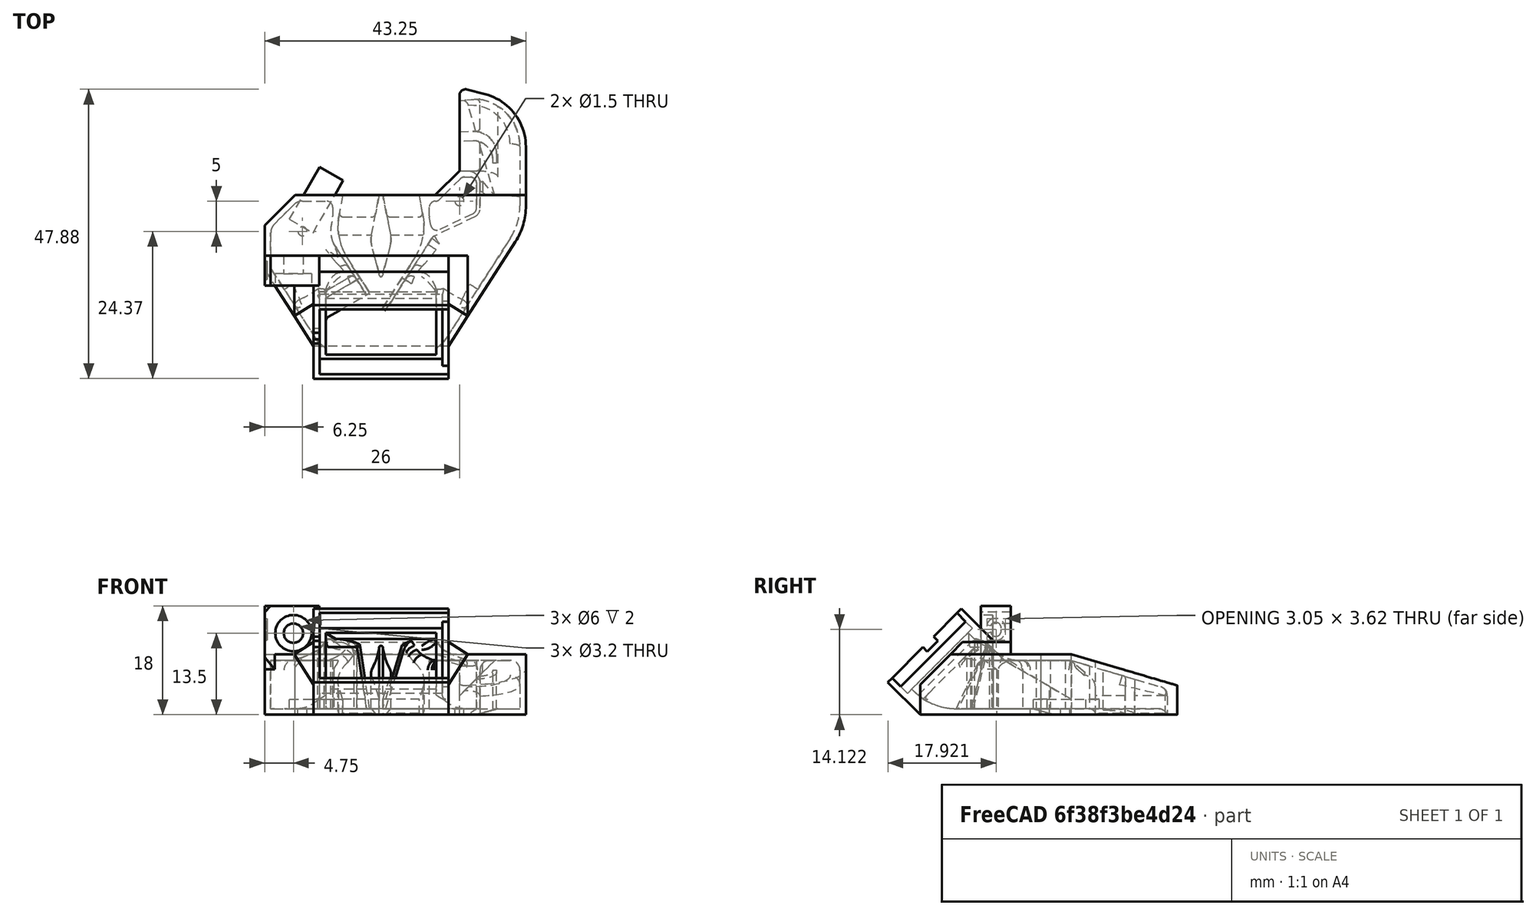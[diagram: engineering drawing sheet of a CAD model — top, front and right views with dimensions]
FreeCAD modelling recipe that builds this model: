
FCSTD DOCUMENT  (FreeCAD 0.18R16146 (Git))
Label: duct-lite
License: All rights reserved
LicenseURL: http://en.wikipedia.org/wiki/All_rights_reserved
objects: Part::Box×13, Part::Chamfer×8, Part::MultiFuse×8, Part::Cut×6, Part::Feature×5, Part::Cylinder×2, Part::Fillet×2
note: 44 computed .brp shape members not serialized (recipe doc carries the construction recipe); baked Part::Feature solids carry a one-line shape summary decoded from their .brp

FEATURE [Part::Feature] Part__Feature  label="RHD_nozzle_C_Final"
  Placement = pos=(0,0,0) rot=(1,0,0;1.5708rad)
  shape: bbox 48.02 x 47.91 x 18.02 mm, 273 faces (baked)
FEATURE [Part::Box] Box  label="Cube"
  AttacherType = Attacher::AttachEngine3D
  Height = 12
  Length = 23
  Placement = pos=(-29,4,0) rot=(0,0,1;0rad)
  Width = 21
FEATURE [Part::Box] Box001  label="Cube001"
  AttacherType = Attacher::AttachEngine3D
  Height = 19
  Length = 10
  Placement = pos=(-29.25,-13,0) rot=(0,0,1;0rad)
  Width = 23
FEATURE [Part::Box] Box002  label="Cube002"
  AttacherType = Attacher::AttachEngine3D
  Height = 12
  Length = 23
  Placement = pos=(-29,4,0) rot=(0,0,1;0rad)
  Width = 21
FEATURE [Part::Box] Box003  label="Cube003"
  AttacherType = Attacher::AttachEngine3D
  Height = 19
  Length = 10
  Placement = pos=(-29.25,-13,0) rot=(0,0,1;0rad)
  Width = 23
FEATURE [Part::Cut] Cut
  Base = -> Part__Feature
  Tool = -> Box002
FEATURE [Part::Cut] Cut001
  Base = -> Cut
  Tool = -> Box003
FEATURE [Part::Box] Box004  label="Cube004"
  AttacherType = Attacher::AttachEngine3D
  Height = 16
  Length = 10
  Placement = pos=(-24.25,-1,0) rot=(0,0,1;0rad)
  Width = 10
FEATURE [Part::Chamfer] Chamfer
  Base = -> Box004
  Edges = 1 edges r=5: [Edge5]
FEATURE [Part::Feature] Chamfer001
  shape: bbox 10 x 10 x 16 mm, 7 faces (baked)
FEATURE [Part::Cut] Cut002
  Base = -> Cut001
  Tool = -> Chamfer
FEATURE [Part::Box] Box005  label="Cube005"
  AttacherType = Attacher::AttachEngine3D
  Height = 10
  Length = 1
  Placement = pos=(-19.25,-7,0) rot=(0,0,1;0rad)
  Width = 6
FEATURE [Part::Box] Box006  label="Cube006"
  AttacherType = Attacher::AttachEngine3D
  Height = 10
  Length = 8
  Placement = pos=(-15,3,0) rot=(0,0,1;0rad)
  Width = 1
FEATURE [Part::Box] Box007  label="Cube007"
  AttacherType = Attacher::AttachEngine3D
  Height = 10
  Length = 8
  Placement = pos=(-19.3699,-2.52958,0) rot=(0,0,1;0.785398rad)
  Width = 1
FEATURE [Part::MultiFuse] Fusion001
  Shapes = -> [Chamfer001,Box,Box001]
FEATURE [Part::Cylinder] Cylinder
  Angle = 360
  AttacherType = Attacher::AttachEngine3D
  Height = 3
  Placement = pos=(-13,-2,0) rot=(0,0,1;0rad)
  Radius = 0.75
FEATURE [Part::Box] Box008  label="Cube008"
  AttacherType = Attacher::AttachEngine3D
  Height = 1.57
  Length = 4.5
  Placement = pos=(-15.1532,-0.0125771,1) rot=(0,0,-1;0.523599rad)
  Width = 10
FEATURE [Part::MultiFuse] Fusion
  Shapes = -> [Box005,Box007,Box006]
FEATURE [Part::Cut] Cut003
  Base = -> Fusion
  Tool = -> Fusion001
FEATURE [Part::Fillet] Fillet
  Base = -> Cut003
  Edges = 2 edges r=2: [Edge17,Edge31]
FEATURE [Part::Feature] Body001
  Placement = pos=(0,0,1) rot=(0,0,1;0rad)
  shape: bbox 12.23 x 12.68 x 8 mm, 3 faces (baked)
FEATURE [Part::Cut] Cut004
  Base = -> Cut002
  Tool = -> Body001
FEATURE [Part::Box] Box009  label="Cube009"
  AttacherType = Attacher::AttachEngine3D
  Height = 10
  Length = 1
  Placement = pos=(-19.25,-9,0) rot=(0,0,1;0rad)
  Width = 3
FEATURE [Part::Chamfer] Chamfer002
  Base = -> Box009
  Edges = 1 edges r=0.7: [Edge1]
FEATURE [Part::MultiFuse] Fusion002
  Shapes = -> [Fillet,Chamfer002]
FEATURE [Part::MultiFuse] Fusion003  label="stage-1"
  Shapes = -> [Cut004,Fusion002]
FEATURE [Part::Feature] Fusion003001  label="stage-1-rf"
  shape: bbox 43.62 x 47.91 x 18.02 mm, 215 faces (baked)
FEATURE [Part::Box] Box010  label="Cube010"
  AttacherType = Attacher::AttachEngine3D
  Height = 14
  Length = 7.5
  Placement = pos=(-10,-13.5,0) rot=(0,0,1;0.523599rad)
  Width = 1
FEATURE [Part::Box] Box011  label="Cube011"
  AttacherType = Attacher::AttachEngine3D
  Height = 12
  Length = 1
  Placement = pos=(-10.15,-22,0) rot=(0,0,1;0rad)
  Width = 10
FEATURE [Part::Chamfer] Chamfer003
  Base = -> Box011
  Edges = 1 edges r=1: [Edge9]
FEATURE [Part::Chamfer] Chamfer004
  Base = -> Chamfer003
  Edges = 1 edges r=8: [Edge8]
FEATURE [Part::Chamfer] Chamfer005
  Base = -> Box010
  Edges = 1 edges: [Edge2 r1=1.5 r2=1.8]
FEATURE [Part::Chamfer] Chamfer006
  Base = -> Chamfer005
  Edges = 1 edges: [Edge15 r1=4 r2=2]
FEATURE [Part::Box] Box012  label="Cube012"
  AttacherType = Attacher::AttachEngine3D
  Height = 1
  Length = 16
  Placement = pos=(-10,-19,0) rot=(0,0,1;0rad)
  Width = 10
FEATURE [Part::MultiFuse] Fusion003002
  Shapes = -> [Chamfer006,Box012]
FEATURE [Part::Chamfer] Chamfer007
  Base = -> Fusion003002
  Edges = 1 edges: [Edge5 r1=2.94 r2=10.2]
FEATURE [Part::MultiFuse] Fusion003003
  Shapes = -> [Chamfer004,Chamfer007]
FEATURE [Part::Fillet] Fillet001
  Base = -> Fusion003003
  Edges = 1 edges r=1: [Edge26]
FEATURE [Part::MultiFuse] Fusion003004  label="stage-2"
  Shapes = -> [Fusion003001,Fillet001]
FEATURE [Part::Feature] Fusion003004001  label="stage-2-rf"
  shape: bbox 43.62 x 47.91 x 18.02 mm, 240 faces (baked)
FEATURE [Part::Cylinder] Cylinder001
  Angle = 360
  AttacherType = Attacher::AttachEngine3D
  Height = 3
  Placement = pos=(13,3,0) rot=(0,0,1;0rad)
  Radius = 0.75
FEATURE [Part::MultiFuse] Fusion003004002
  Shapes = -> [Cylinder001,Cylinder]
FEATURE [Part::Cut] Cut005
  Base = -> Fusion003004001
  Tool = -> Fusion003004002
FEATURE [Part::Chamfer] Chamfer008  label="stage-3"
  Base = -> Cut005
  Edges = 1 edges r=1: [Edge7]
